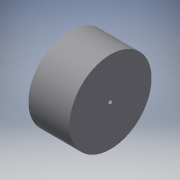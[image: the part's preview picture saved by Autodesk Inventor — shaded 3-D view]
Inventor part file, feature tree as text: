
AUTODESK INVENTOR PART (.ipt)
format: ipt  version: 2019 (Build 230136000, 136)  size: 96,768 bytes
history: native  units: in
note: dims shown in document units (in); Inventor stores cm internally (conversion verified against a paired STEP export)
features: extrude x1, sketch x1
ambient origin geometry x8: Origin, YZ Plane, XZ Plane, XY Plane, X Axis, Y Axis, Z Axis, Center Point
bodies: Solid1 (feature_tree)
feature tree (2):
  extrude  "Extrusion1"  Depth=2.5in
  sketch  "Sketch1"  dims[d0=0.5in d1=10.0in d2=2.5in d3=0.0in]
